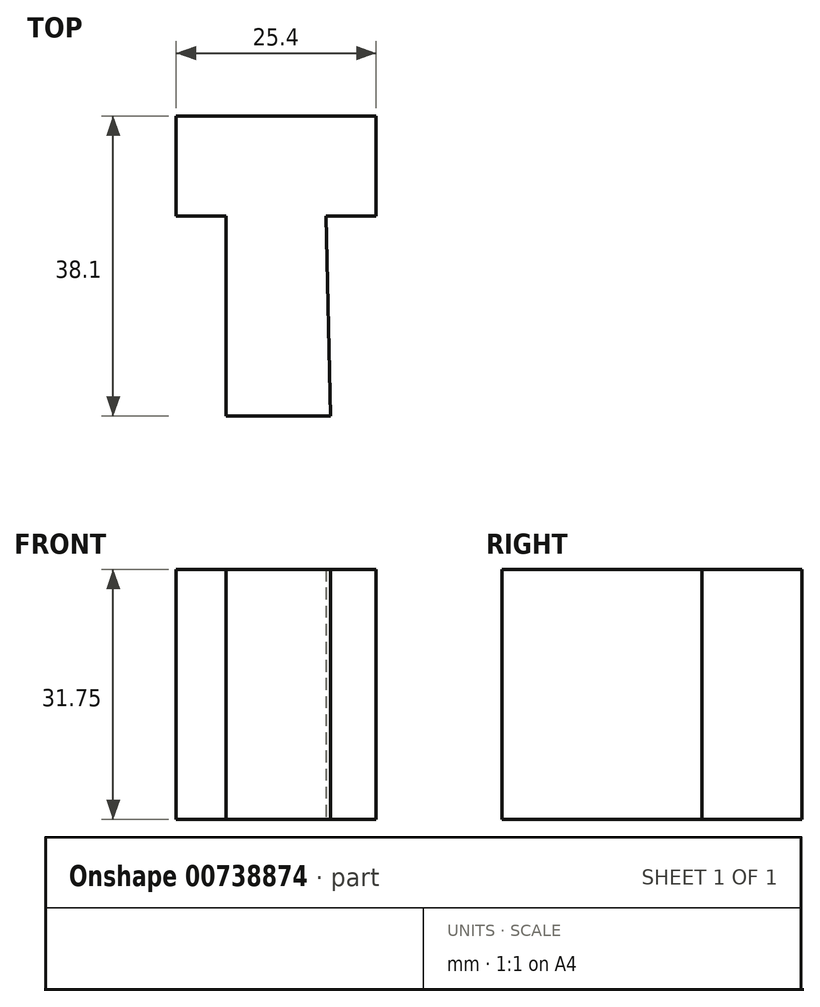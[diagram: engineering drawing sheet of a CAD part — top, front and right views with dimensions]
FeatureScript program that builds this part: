
annotation { "Feature Type Name" : "Feature", "Feature Type Description" : "" }
export const myFeature = defineFeature(function(context is Context, id is Id, definition is map)
    precondition{}
    {
        {
            var Q0;
            Q0=qCreatedBy(makeId("Top.planeOp"),FACE);
            var sketch = newSketch(context, id + "F0", { "sketchPlane" : qUnion([Q0])});
            skLineSegment(sketch, "E0", {"start": v(-19.05, 38.1) * mm, "end": v(6.35, 38.1) * mm});
            skLineSegment(sketch, "E1", {"start": v(6.35, 38.1) * mm, "end": v(6.35, 25.4) * mm});
            skLineSegment(sketch, "E2", {"start": v(6.35, 25.4) * mm, "end": v(0, 25.4) * mm});
            skLineSegment(sketch, "E3", {"start": v(-19.05, 38.1) * mm, "end": v(-19.05, 25.4) * mm});
            skLineSegment(sketch, "E4", {"start": v(-19.05, 25.4) * mm, "end": v(-19.05, 25.4) * mm});
            skLineSegment(sketch, "E5", {"start": v(-19.05, 25.4) * mm, "end": v(-12.7, 25.4) * mm});
            skLineSegment(sketch, "E6", {"start": v(-12.7, 25.4) * mm, "end": v(-12.7, 0) * mm});
            skLineSegment(sketch, "E7", {"start": v(-12.7, 0) * mm, "end": v(0, 0) * mm});
            skLineSegment(sketch, "E8", {"start": v(0, 0) * mm, "end": v(0.57, 0) * mm});
            skLineSegment(sketch, "E9", {"start": v(0.57, 0) * mm, "end": v(0, 25.4) * mm});
            skSolve(sketch);
        }
        {
            var Q0;
            Q0=makeQuery(id+"F0.imprint","IMPRINT",FACE,{"disambiguationData":[TD([[makeQuery(id+"F0.imprint","IMPRINT",EDGE,{"derivedFrom":sQuery(id+"F0.wireOp",EDGE,"E0")}),-1.0]])]});
            extrude(context, id + "F1", {"entities" : qUnion([Q0]), "depth" : 31.75 * mm, "offsetDistance" : 25.4 * mm});
        }
    });
